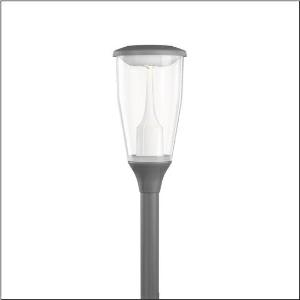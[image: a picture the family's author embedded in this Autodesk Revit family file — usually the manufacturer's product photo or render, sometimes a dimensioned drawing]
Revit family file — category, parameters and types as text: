
# Revit family: dl_11_iq___p1_0a_5xa5565bf14h000022_0962
name_source: partatom
category: Lighting Fixtures
units: mm (PartAtom-declared; Revit-internal decimal feet)

## family parameters
Cut with Voids When Loaded = No
Host = Face
Light Source = No
Part Type = Normal
Room Calculation Point = No
Round Connector Dimension = Use Diameter
Shared = No

## types (1)
- --- (1 x LED, 1530 lm, 12.9 W, 2200K)
    Apparent Load = 13 VA
    CIE Flux Codes = 34 63 91 95 100
    Color Rendering = 70
    Color Temperature = 2200K
    Default Elevation = 1800 mm
    Description = DL 11 iQ, mast luminaire, Module 540 iQ-SR, primary light control with 3 zone facetted reflector, of plastic, silver coated, highly specular, structured, primary optical cover: cover, of PMMA, transparent, light distribution: P1.0a, light emission: direct distribution, primary light characteristic: asymmetric, installation type: post-top, LED, High Power LED, rated luminous flux: 1.560lm, luminous efficacy: 149lm/W, light colour: 722, colour temperature: 2200K, control: Street-Remote, Auto-Match, Temp-Guard, Lumen-Switch, Night-Set, Smart-Wire, Light-Fading, Desk-Remote (wireless, voltage-free reading and setting of iQ features in the workshop via application-optimized NFC function/RFID function), optimised constant luminous flux control (CLO 2.0), mains connection: 220..240V, AC, 50/60Hz, connection cable pre-assembled, cable length: 5,5m, start of lifetime: 13W, end of service life: 13W, reduction: 5W, luminaire housing, upper part, of diecast aluminium, coated, Siteco® metallic grey (DB 702S), spigot size: 60mm (post-top), post-top mast mounting element, of diecast aluminium, coated, Siteco® metallic grey (DB 702S), Module 540 iQ-SR, traffic white (RAL 9016), equipment: standard, protection rating (complete): IP66, insulation class (complete): insulation class II (safety insulation), certification: CE, ENEC, ENEC+, VDE, packaging unit: 1 piece

Light Distribution: P1.0a
    Height = 665 mm
    Lamp = 1 x LED
    Lamp Light Flux = 1530 lm
    Lamp Power = 12.9 W
    Lamp count = 1
    Length = 334 mm
    Luminous efficacy = 119 lm/W
    Manufacturer = Siteco
    ModVariant = No
    Model = 5XA5565BF14H000022
    Number of Poles = 1
    OnlyDefault = Yes
    Power Factor = 1
    Product Name = DL 11 iQ | P1.0a
    Product group = mast luminaire | pylon top
    ProductGroupID = 6100
    Protection Class = Protection class II
    Protection Degree = IP 66
    RLX_Detail_Level = 1
    RLX_Emergency_Light_Flux = 0 lm
    RLX_Emergency_Type = 0
    RLX_Emergency_Type_DB = No
    RlxData = <blob elided: 103557 chars, md5=1703e118>
    Socket = socket
    Standby Power = 0 W
    System Light Flux = 1530 lm
    System Power = 13 W
    Type Comments = factory setting: luminous flux: 100 % | dim-lin: 254 | 516 mA
    Type Image = l_1258354.jpg
    URL = http://relux.com
    VarID = @adj_042469
    Voltage = 0 V
    Weight = 0.00 kg
    Width = 0 mm  [stored 0 ft]

note: [stored X ft] marks values corroborated as IEEE doubles in the binary element streams (Revit-internal decimal feet)

## geometry (parser evidence)
native form markers: Blend x4, Sweep x9
no freeform markers — native parametric forms only
